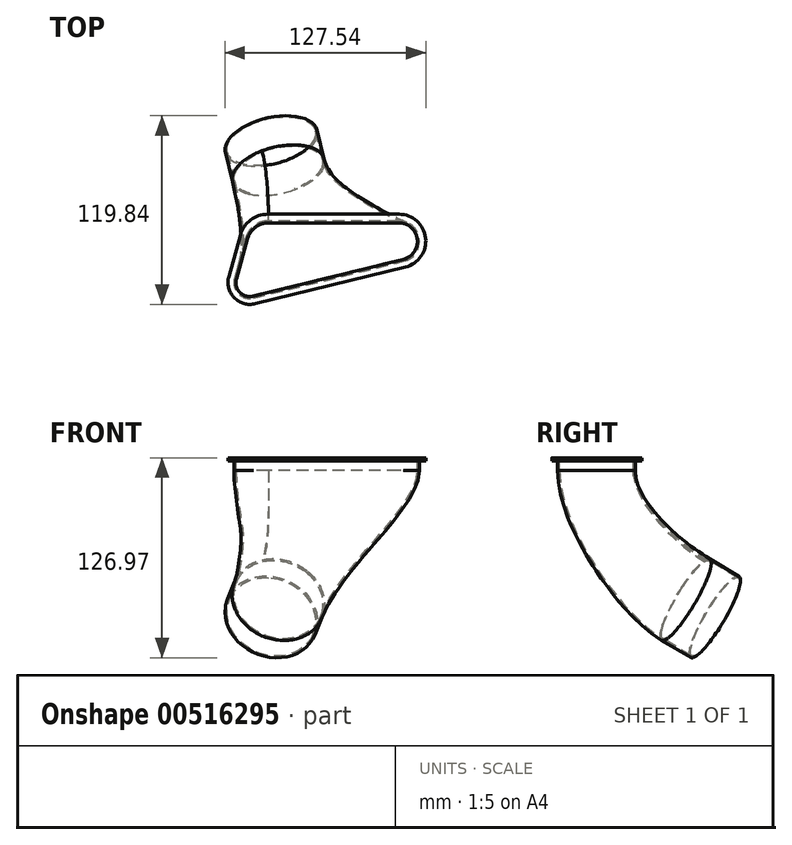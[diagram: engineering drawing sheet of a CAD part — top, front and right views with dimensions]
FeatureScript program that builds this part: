
annotation { "Feature Type Name" : "Feature", "Feature Type Description" : "" }
export const myFeature = defineFeature(function(context is Context, id is Id, definition is map)
    precondition{}
    {
        {
            var Q0;
            Q0=qCreatedBy(makeId("Top.planeOp"),FACE);
            var sketch = newSketch(context, id + "F0", { "sketchPlane" : qUnion([Q0])});
            skLineSegment(sketch, "E0", {"start": v(-17.27, 22.77) * mm, "end": v(65.53, 22.77) * mm});
            skLineSegment(sketch, "E1", {"start": v(68.62, -2.86) * mm, "end": v(-26.76, -26.2) * mm});
            skLineSegment(sketch, "E2", {"start": v(-38.78, -13.84) * mm, "end": v(-31.73, 11.75) * mm});
            skPoint(sketch, "E3.visualSharp", {"position": v(173.3, 22.77) * mm});
            skArc(sketch, "E3.filletArc", {"start": v(68.62, -2.86) * mm, "mid": v(78.44, 11.33) * mm, "end": v(65.53, 22.77) * mm});
            skPoint(sketch, "E4.visualSharp", {"position": v(-28.7, 22.77) * mm});
            skArc(sketch, "E4.filletArc", {"start": v(-17.27, 22.77) * mm, "mid": v(-26.36, 19.7) * mm, "end": v(-31.73, 11.75) * mm});
            skPoint(sketch, "E5.visualSharp", {"position": v(-43.3, -30.26) * mm});
            skArc(sketch, "E5.filletArc", {"start": v(-38.78, -13.84) * mm, "mid": v(-36.3, -23.46) * mm, "end": v(-26.76, -26.2) * mm});
            skSolve(sketch);
        }
        {
            var Q0;
            Q0 = qSketchRegion(id + "F0", true);
            extrude(context, id + "F1", {"entities" : qUnion([Q0]), "oppositeDirection" : true, "depth" : 6 * mm, "offsetDistance" : 25 * mm});
        }
        {
            var Q0;
            Q0=makeQuery(id+"F1.opExtrude","CAP_FACE",FACE,{"disambiguationData":[OSD([sQuery(id+"F0.wireOp",EDGE,"E0"),sQuery(id+"F0.wireOp",EDGE,"E1"),sQuery(id+"F0.wireOp",EDGE,"E2"),sQuery(id+"F0.wireOp",EDGE,"E3.filletArc"),sQuery(id+"F0.wireOp",EDGE,"E4.filletArc"),sQuery(id+"F0.wireOp",EDGE,"E5.filletArc")])],"isStart":false});
            var sketch = newSketch(context, id + "F2", { "sketchPlane" : qUnion([Q0])});
            skCircle(sketch, "E6", {"center": v(0, -60) * mm, "radius": 30 * mm});
            skSolve(sketch);
        }
        {
            var Q0;
            Q0 = qSketchRegion(id + "F2", true);
            extrude(context, id + "F3", {"entities" : qUnion([Q0]), "depth" : 100 * mm, "offsetDistance" : 25 * mm});
        }
        {
            var Q0;
            Q0=makeQuery(id+"F3.opExtrude","CAP_FACE",FACE,{"disambiguationData":[OSD([sQuery(id+"F2.wireOp",EDGE,"E6")])],"isStart":true});
            extrude(context, id + "F4", {"entities" : qUnion([Q0]), "operationType" : NewBodyOperationType.REMOVE, "oppositeDirection" : true, "depth" : 98 * mm, "offsetDistance" : 25 * mm});
        }
        {
            var Q0;
            Q0=makeQuery(id+"F3.opExtrude","SWEPT_BODY",BODY,{"disambiguationData":[OSD([sQuery(id+"F2.wireOp",EDGE,"E6")])]});
            var Q1;
            Q1=makeQuery(id+"F1.opExtrude","CAP_EDGE",EDGE,{"disambiguationData":[OSD([sQuery(id+"F0.wireOp",EDGE,"E1")])],"isStart":false});
            transform(context, id + "F5", {"entities" : qUnion([Q0]), "transformType" : TransformType.ROTATION, "transformAxis" : qUnion([Q1]), "angle" : 60 * degree, "oppositeDirection" : true, "makeCopy" : false});
        }
        {
            var Q0;
            Q0=makeQuery(id+"F3.opExtrude","SWEPT_BODY",BODY,{"disambiguationData":[OSD([sQuery(id+"F2.wireOp",EDGE,"E6")])]});
            transform(context, id + "F6", {"entities" : qUnion([Q0]), "transformType" : TransformType.TRANSLATION_3D, "dx" : 0 * mm, "dy" : -50 * mm, "dz" : -100 * mm, "makeCopy" : false});
        }
        {
            var Q1;
            Q1=makeQuery(id+"F1.opExtrude","CAP_FACE",FACE,{"disambiguationData":[OSD([sQuery(id+"F0.wireOp",EDGE,"E0"),sQuery(id+"F0.wireOp",EDGE,"E1"),sQuery(id+"F0.wireOp",EDGE,"E2"),sQuery(id+"F0.wireOp",EDGE,"E3.filletArc"),sQuery(id+"F0.wireOp",EDGE,"E4.filletArc"),sQuery(id+"F0.wireOp",EDGE,"E5.filletArc")])],"isStart":false});
            var Q2;
            Q2=makeQuery(id+"F4.boolean.opBoolean","COPY",FACE,{"derivedFrom":makeQuery(id+"F4.opExtrude","CAP_FACE",FACE,{"disambiguationData":[OSD([sQuery(id+"F2.wireOp",EDGE,"E6")])],"isStart":false})});
            loft(context, id + "F7", {"operationType" : NewBodyOperationType.ADD, "startCondition" : LoftEndDerivativeType.NORMAL_TO_PROFILE, "startMagnitude" : 1, "endCondition" : LoftEndDerivativeType.NORMAL_TO_PROFILE, "endMagnitude" : 1, "sheetProfilesArray" : [{ "sheetProfileEntities" : qUnion([Q1]) }, { "sheetProfileEntities" : qUnion([Q2]) }]});
        }
        {
            var Q0;
            Q0=makeQuery(id+"F3.opExtrude","CAP_FACE",FACE,{"disambiguationData":[OSD([sQuery(id+"F2.wireOp",EDGE,"E6")])],"isStart":false});
            var Q1;
            Q1=makeQuery(id+"F1.opExtrude","CAP_FACE",FACE,{"disambiguationData":[OSD([sQuery(id+"F0.wireOp",EDGE,"E0"),sQuery(id+"F0.wireOp",EDGE,"E1"),sQuery(id+"F0.wireOp",EDGE,"E2"),sQuery(id+"F0.wireOp",EDGE,"E3.filletArc"),sQuery(id+"F0.wireOp",EDGE,"E4.filletArc"),sQuery(id+"F0.wireOp",EDGE,"E5.filletArc")])],"isStart":true});
            shell(context, id + "F8", {"entities" : qUnion([Q0, Q1]), "thickness" : 1.2 * mm});
        }
        {
            var Q0;
            Q0=makeQuery(id+"F3.opExtrude","CAP_FACE",FACE,{"disambiguationData":[OSD([sQuery(id+"F2.wireOp",EDGE,"E6")])],"isStart":false});
            extrude(context, id + "F9", {"entities" : qUnion([Q0]), "operationType" : NewBodyOperationType.ADD, "depth" : 20 * mm, "offsetDistance" : 25 * mm});
        }
        {
            var Q0;
            Q0=makeQuery(id+"F1.opExtrude","CAP_FACE",FACE,{"disambiguationData":[OSD([sQuery(id+"F0.wireOp",EDGE,"E0"),sQuery(id+"F0.wireOp",EDGE,"E1"),sQuery(id+"F0.wireOp",EDGE,"E2"),sQuery(id+"F0.wireOp",EDGE,"E3.filletArc"),sQuery(id+"F0.wireOp",EDGE,"E4.filletArc"),sQuery(id+"F0.wireOp",EDGE,"E5.filletArc")])],"isStart":true});
            extrude(context, id + "F10", {"entities" : qUnion([Q0]), "operationType" : NewBodyOperationType.ADD, "depth" : 2 * mm, "offsetDistance" : 25 * mm});
        }
        {
            var Q0;
            Q0=makeQuery(id+"F10.opExtrude","CAP_FACE",FACE,{"disambiguationData":[OSD([sQuery(id+"F0.wireOp",EDGE,"E0"),sQuery(id+"F0.wireOp",EDGE,"E1"),sQuery(id+"F0.wireOp",EDGE,"E2"),sQuery(id+"F0.wireOp",EDGE,"E3.filletArc"),sQuery(id+"F0.wireOp",EDGE,"E4.filletArc"),sQuery(id+"F0.wireOp",EDGE,"E5.filletArc")])],"isStart":false});
            var sketch = newSketch(context, id + "F11", { "sketchPlane" : qUnion([Q0])});
            skLineSegment(sketch, "E7", {"start": v(-25.6, -29.85) * mm, "end": v(69.7, -6.51) * mm});
            skLineSegment(sketch, "E8", {"start": v(65.67, 27) * mm, "end": v(-17.73, 27) * mm});
            skLineSegment(sketch, "E9", {"start": v(-35.07, 13.84) * mm, "end": v(-42.42, -12.48) * mm});
            skPoint(sketch, "E10.visualSharp", {"position": v(-48.85, -35.54) * mm});
            skArc(sketch, "E10.filletArc", {"start": v(-42.42, -12.48) * mm, "mid": v(-39, -25.99) * mm, "end": v(-25.6, -29.85) * mm});
            skPoint(sketch, "E11.visualSharp", {"position": v(-31.4, 27) * mm});
            skArc(sketch, "E11.filletArc", {"start": v(-17.73, 27) * mm, "mid": v(-28.62, 23.34) * mm, "end": v(-35.07, 13.84) * mm});
            skPoint(sketch, "E12.visualSharp", {"position": v(206.6, 27) * mm});
            skArc(sketch, "E12.filletArc", {"start": v(69.7, -6.51) * mm, "mid": v(82.54, 12.04) * mm, "end": v(65.67, 27) * mm});
            skLineSegment(sketch, "E13", {"start": v(-37.62, -14.16) * mm, "end": v(-30.57, 11.43) * mm});
            skLineSegment(sketch, "E14", {"start": v(-27.04, -25.04) * mm, "end": v(68.33, -1.7) * mm});
            skLineSegment(sketch, "E15", {"start": v(65.53, 21.57) * mm, "end": v(-17.27, 21.57) * mm});
            skArc(sketch, "E16", {"start": v(-17.27, 21.57) * mm, "mid": v(-25.63, 18.75) * mm, "end": v(-30.57, 11.43) * mm});
            skArc(sketch, "E17", {"start": v(-37.62, -14.16) * mm, "mid": v(-35.45, -22.63) * mm, "end": v(-27.04, -25.04) * mm});
            skArc(sketch, "E18", {"start": v(68.33, -1.7) * mm, "mid": v(77.24, 11.18) * mm, "end": v(65.53, 21.57) * mm});
            skSolve(sketch);
        }
        {
            var Q0;
            Q0 = qSketchRegion(id + "F11", true);
            extrude(context, id + "F12", {"entities" : qUnion([Q0]), "operationType" : NewBodyOperationType.ADD, "oppositeDirection" : true, "depth" : 2 * mm, "offsetDistance" : 25 * mm});
        }
        {
            var Q0;
            {var subQ0=sQuery(id+"F0.wireOp",EDGE,"E0");Q0=makeQuery(id+"F10.opExtrude","CAP_EDGE",EDGE,{"disambiguationData":[OSD([subQ0]),TDD([makeQuery(id+"F8.opShell","OFFSET_EDGE",EDGE,{"disambiguationData":[OSD([subQ0])]})])],"isStart":false});}
            fillet(context, id + "F13", {"entities" : qUnion([Q0]), "radius" : 3 * mm, "tangentPropagation" : true, "allowEdgeOverflow" : false});
        }
    });
